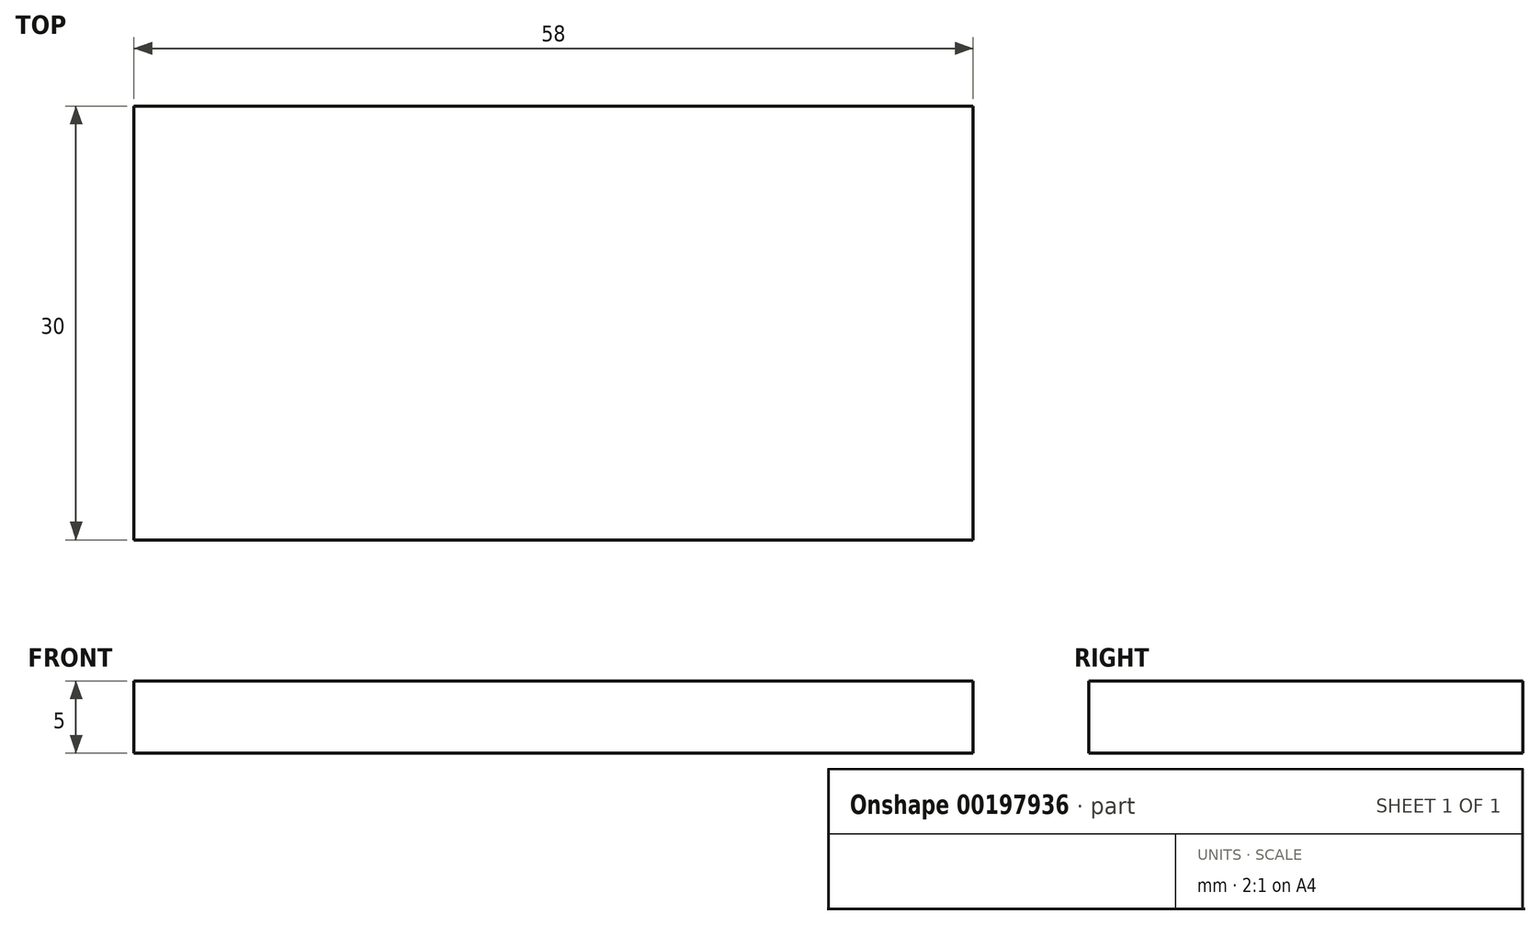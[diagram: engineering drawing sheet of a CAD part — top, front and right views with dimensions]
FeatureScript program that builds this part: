
annotation { "Feature Type Name" : "Feature", "Feature Type Description" : "" }
export const myFeature = defineFeature(function(context is Context, id is Id, definition is map)
    precondition{}
    {
        {
            var Q0;
            Q0=qCreatedBy(makeId("Top.planeOp"),FACE);
            var sketch = newSketch(context, id + "F0", { "sketchPlane" : qUnion([Q0])});
            skLineSegment(sketch, "E0.bottom", {"start": v(-24.95, 30) * mm, "end": v(33.05, 30) * mm});
            skLineSegment(sketch, "E0.top", {"start": v(-24.95, 0) * mm, "end": v(33.05, 0) * mm});
            skLineSegment(sketch, "E0.left", {"start": v(-24.95, 30) * mm, "end": v(-24.95, 0) * mm});
            skLineSegment(sketch, "E0.right", {"start": v(33.05, 30) * mm, "end": v(33.05, 0) * mm});
            skLineSegment(sketch, "E1.bottom", {"start": v(-24.95, 0) * mm, "end": v(-19.95, 0) * mm});
            skLineSegment(sketch, "E1.top", {"start": v(-24.95, -36.6) * mm, "end": v(-19.95, -36.6) * mm});
            skLineSegment(sketch, "E1.left", {"start": v(-24.95, 0) * mm, "end": v(-24.95, -36.6) * mm});
            skLineSegment(sketch, "E1.right", {"start": v(-19.95, 0) * mm, "end": v(-19.95, -36.6) * mm});
            skLineSegment(sketch, "E2.bottom", {"start": v(33.05, 0) * mm, "end": v(28.04, 0) * mm});
            skLineSegment(sketch, "E2.top", {"start": v(33.05, -36.6) * mm, "end": v(28.04, -36.6) * mm});
            skLineSegment(sketch, "E2.left", {"start": v(33.05, 0) * mm, "end": v(33.05, -36.6) * mm});
            skLineSegment(sketch, "E2.right", {"start": v(28.04, 0) * mm, "end": v(28.04, -36.6) * mm});
            skSolve(sketch);
        }
        {
            var Q0;
            Q0=makeQuery(id+"F0.imprint","IMPRINT",FACE,{"disambiguationData":[TD([[makeQuery(id+"F0.imprint","IMPRINT",EDGE,{"derivedFrom":sQuery(id+"F0.wireOp",EDGE,"E0.bottom")}),-1.0]])]});
            var Q1;
            Q1=makeQuery(id+"F0.imprint","IMPRINT",FACE,{"disambiguationData":[TD([[makeQuery(id+"F0.imprint","IMPRINT",EDGE,{"derivedFrom":sQuery(id+"F0.wireOp",EDGE,"E1.bottom")}),-1.0]])]});
            var Q2;
            Q2=makeQuery(id+"F0.imprint","IMPRINT",FACE,{"disambiguationData":[TD([[makeQuery(id+"F0.imprint","IMPRINT",EDGE,{"derivedFrom":sQuery(id+"F0.wireOp",EDGE,"E2.bottom")}),1.0]])]});
            extrude(context, id + "F1", {"entities" : qUnion([Q0, Q1, Q2]), "depth" : 5 * mm});
        }
        {
            var Q0;
            Q0=makeQuery(id+"F1.opExtrude","CAP_FACE",FACE,{"disambiguationData":[OSD([sQuery(id+"F0.wireOp",EDGE,"E0.bottom"),sQuery(id+"F0.wireOp",EDGE,"E0.top"),sQuery(id+"F0.wireOp",EDGE,"E0.left"),sQuery(id+"F0.wireOp",EDGE,"E0.right"),sQuery(id+"F0.wireOp",EDGE,"E1.top"),sQuery(id+"F0.wireOp",EDGE,"E1.left"),sQuery(id+"F0.wireOp",EDGE,"E1.right"),sQuery(id+"F0.wireOp",EDGE,"E2.top"),sQuery(id+"F0.wireOp",EDGE,"E2.left"),sQuery(id+"F0.wireOp",EDGE,"E2.right")])],"isStart":false});
            var sketch = newSketch(context, id + "F2", { "sketchPlane" : qUnion([Q0])});
            skLineSegment(sketch, "E3", {"start": v(-22.45, -36.6) * mm, "end": v(-22.45, -27.58) * mm, "construction": true});
            skLineSegment(sketch, "E4", {"start": v(-22.45, -27.58) * mm, "end": v(-24.95, -27.58) * mm, "construction": true});
            skLineSegment(sketch, "E5.bottom", {"start": v(-24.95, -27.58) * mm, "end": v(-19.95, -27.58) * mm});
            skLineSegment(sketch, "E5.top", {"start": v(-24.95, -22.58) * mm, "end": v(-19.95, -22.58) * mm});
            skLineSegment(sketch, "E5.left", {"start": v(-24.95, -27.58) * mm, "end": v(-24.95, -22.58) * mm});
            skLineSegment(sketch, "E5.right", {"start": v(-19.95, -27.58) * mm, "end": v(-19.95, -22.58) * mm});
            skLineSegment(sketch, "E6", {"start": v(-24.95, -22.58) * mm, "end": v(33.05, -22.58) * mm, "construction": true});
            skLineSegment(sketch, "E7", {"start": v(-24.95, -27.58) * mm, "end": v(33.05, -27.58) * mm, "construction": true});
            skLineSegment(sketch, "E8.bottom", {"start": v(28.04, -22.58) * mm, "end": v(33.05, -22.58) * mm});
            skLineSegment(sketch, "E8.top", {"start": v(28.04, -27.58) * mm, "end": v(33.05, -27.58) * mm});
            skLineSegment(sketch, "E8.left", {"start": v(28.04, -22.58) * mm, "end": v(28.04, -27.58) * mm});
            skLineSegment(sketch, "E8.right", {"start": v(33.05, -22.58) * mm, "end": v(33.05, -27.58) * mm});
            skLineSegment(sketch, "E9", {"start": v(4.04, 0) * mm, "end": v(4.04, 30) * mm, "construction": true});
            skLineSegment(sketch, "E10", {"start": v(4.04, 30) * mm, "end": v(-24.95, 4.84) * mm, "construction": true});
            skLineSegment(sketch, "E11", {"start": v(-24.95, 4.84) * mm, "end": v(4.04, 0) * mm, "construction": true});
            skLineSegment(sketch, "E12", {"start": v(4.04, 0) * mm, "end": v(33.05, 27.5) * mm, "construction": true});
            skLineSegment(sketch, "E13", {"start": v(33.05, 27.5) * mm, "end": v(4.04, 30) * mm, "construction": true});
            skLineSegment(sketch, "E14", {"start": v(-10.45, 17.42) * mm, "end": v(18.55, 13.75) * mm, "construction": true});
            skText(sketch, "E15", { "text": "The Rubin\'s\n Workshop", "fontName": "RobotoSlab-Bold.ttf"});
            const initialGuessF2  = {"E15": [-0.01045, 0.01375, 1, 0, 0.00367]};
            skSetInitialGuess(sketch, initialGuessF2);
            skSolve(sketch);
        }
        {
            var Q0;
            Q0 = qConstructionFilter(qBodyType(qCreatedBy(id + "F2" ,EDGE), BodyType.WIRE), ConstructionObject.NO);
            extrude(context, id + "F3", {"bodyType" : ToolBodyType.SURFACE, "surfaceEntities" : qUnion([Q0]), "depth" : 2.5 * mm});
        }
    });
